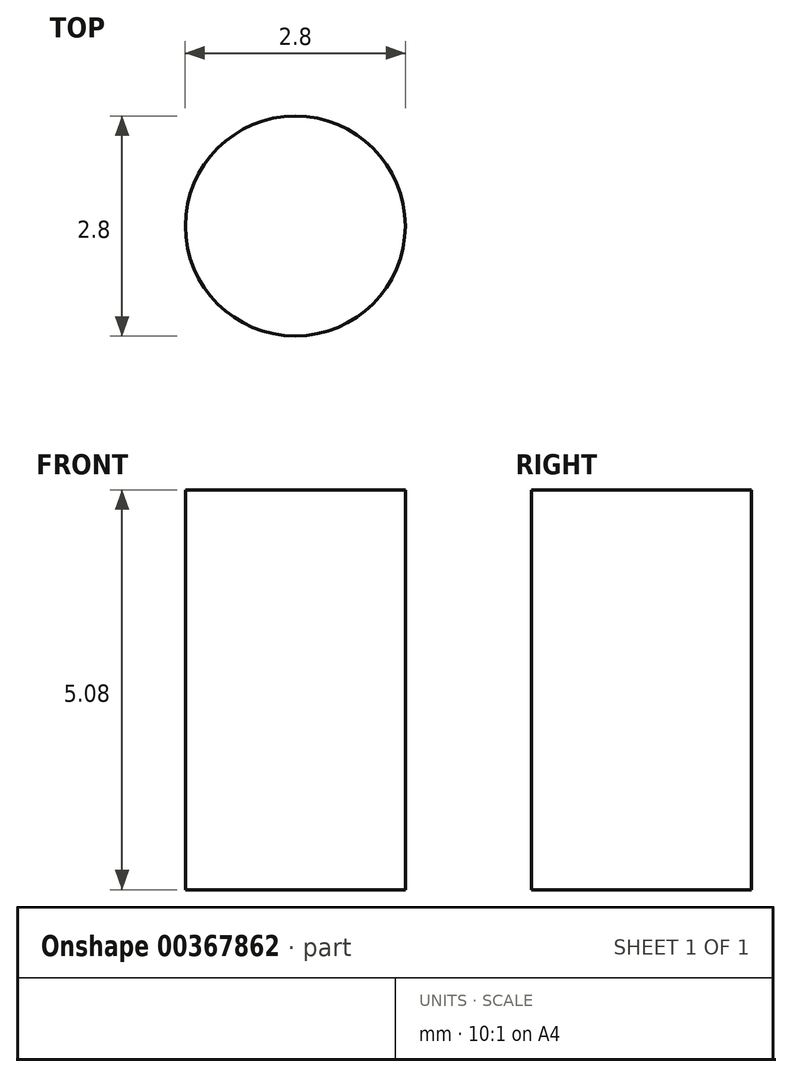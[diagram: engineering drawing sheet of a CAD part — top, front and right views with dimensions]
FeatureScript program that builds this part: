
annotation { "Feature Type Name" : "Feature", "Feature Type Description" : "" }
export const myFeature = defineFeature(function(context is Context, id is Id, definition is map)
    precondition{}
    {
        {
            var Q0;
            Q0=qCreatedBy(makeId("Top.planeOp"),FACE);
            var sketch = newSketch(context, id + "F0", { "sketchPlane" : qUnion([Q0])});
            skCircle(sketch, "E0", {"center": v(0, 0) * mm, "radius": 1.4 * mm});
            skSolve(sketch);
        }
        {
            var Q0;
            Q0 = qSketchRegion(id + "F0", true);
            extrude(context, id + "F1", {"entities" : qUnion([Q0]), "depth" : 5.08 * mm});
        }
    });
